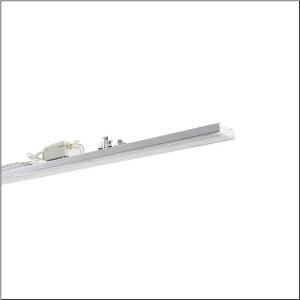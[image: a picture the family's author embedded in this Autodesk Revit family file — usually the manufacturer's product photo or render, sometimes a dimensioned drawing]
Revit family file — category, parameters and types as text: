
# Revit family: licross_r__21_recessed_mo_52tl12dv4fxg3s_6da0
name_source: partatom
category: Lighting Fixtures
units: mm (PartAtom-declared; Revit-internal decimal feet)

## family parameters
Cut with Voids When Loaded = No
Host = Face
Light Source = No
Part Type = Normal
Room Calculation Point = No
Round Connector Dimension = Use Diameter
Shared = No

## types (1)
- --- (1 x LED, 950 lm, 5.5 W, 4000K)
    Apparent Load = 6 VA
    CIE Flux Codes = 72 92 99 100 100
    Color Rendering = 80
    Color Temperature = 4000K
    Default Elevation = 1800 mm
    Description = Licross® 21 Recessed MO, luminaire insert, of sheet steel, galvanised, coil coated, white, length: 2.250mm, width: 66mm, height: 67mm, LED rated luminous flux: 15.420lm, light colour: 840, control gear: DALI 2, with plug, 6-pole, with phase selection, for trunking rail, 14-core, mains connection: 220..240V, AC, 50/60Hz, rated input power: 89W, for trunking rail, 14-core, halogen-free wiring, for emergency light function, converter,control gear: single battery element, battery: LiFeP04, 9Ah, primary optical cover: cover, of PMMA, light emission: direct distribution, primary light characteristic: symmetric, protection rating (complete): IP40, insulation class (complete): insulation class I (protective earthing), certification: CE, UKCA, protection symbol: D if used in an environment without relevant dust loads with corresponding accessories, impact resistance: IK06, permissible ambient temperature for indoor applications: +5..+35°C, standard: EN 60598-2-22, LABS conformity tested according to VDMA 24364:2018-05, reducing of maximum allowable ambient temperature of 5°C with ceiling mounting, corresponds to IFS (International Featured Standards) requirements for safety and quality in the food industry, packaging unit: 1 piece
    Height = 58 mm
    Lamp = 1 x LED
    Lamp Light Flux = 950 lm
    Lamp Power = 5.5 W
    Lamp count = 1
    Length = 2250 mm
    Luminous efficacy = 173 lm/W
    Manufacturer = Siteco
    ModVariant = No
    Model = 52TL12DV4FXG3S
    Mounting Place = Ceiling
    Mounting Type = Pendant
    Number of Poles = 1
    OnlyDefault = Yes
    Power Factor = 1
    Product Name = Licross® 21 Recessed MO
    Product group = luminaire insert
    ProductGroupID = 901
    Protection Class = Protection class I
    Protection Degree = IP 40
    RLX_Detail_Level = 1
    RLX_Emergency_Light_Flux = 0 lm
    RLX_Emergency_Type = 0
    RLX_Emergency_Type_DB = No
    RlxData = <blob elided: 29825 chars, md5=00604572>
    Socket = socket
    Standby Power = 0 W
    System Light Flux = 950 lm
    System Power = 6 W
    Type Comments = : emergency light operation: 3 h
    Type Image = l_1296930.jpg
    URL = http://relux.com
    VarID = @adj_040199
    Voltage = 0 V
    Weight = 0.00 kg
    Width = 66 mm

## geometry (parser evidence)
native form markers: Blend x4, Sweep x11
no freeform markers — native parametric forms only
